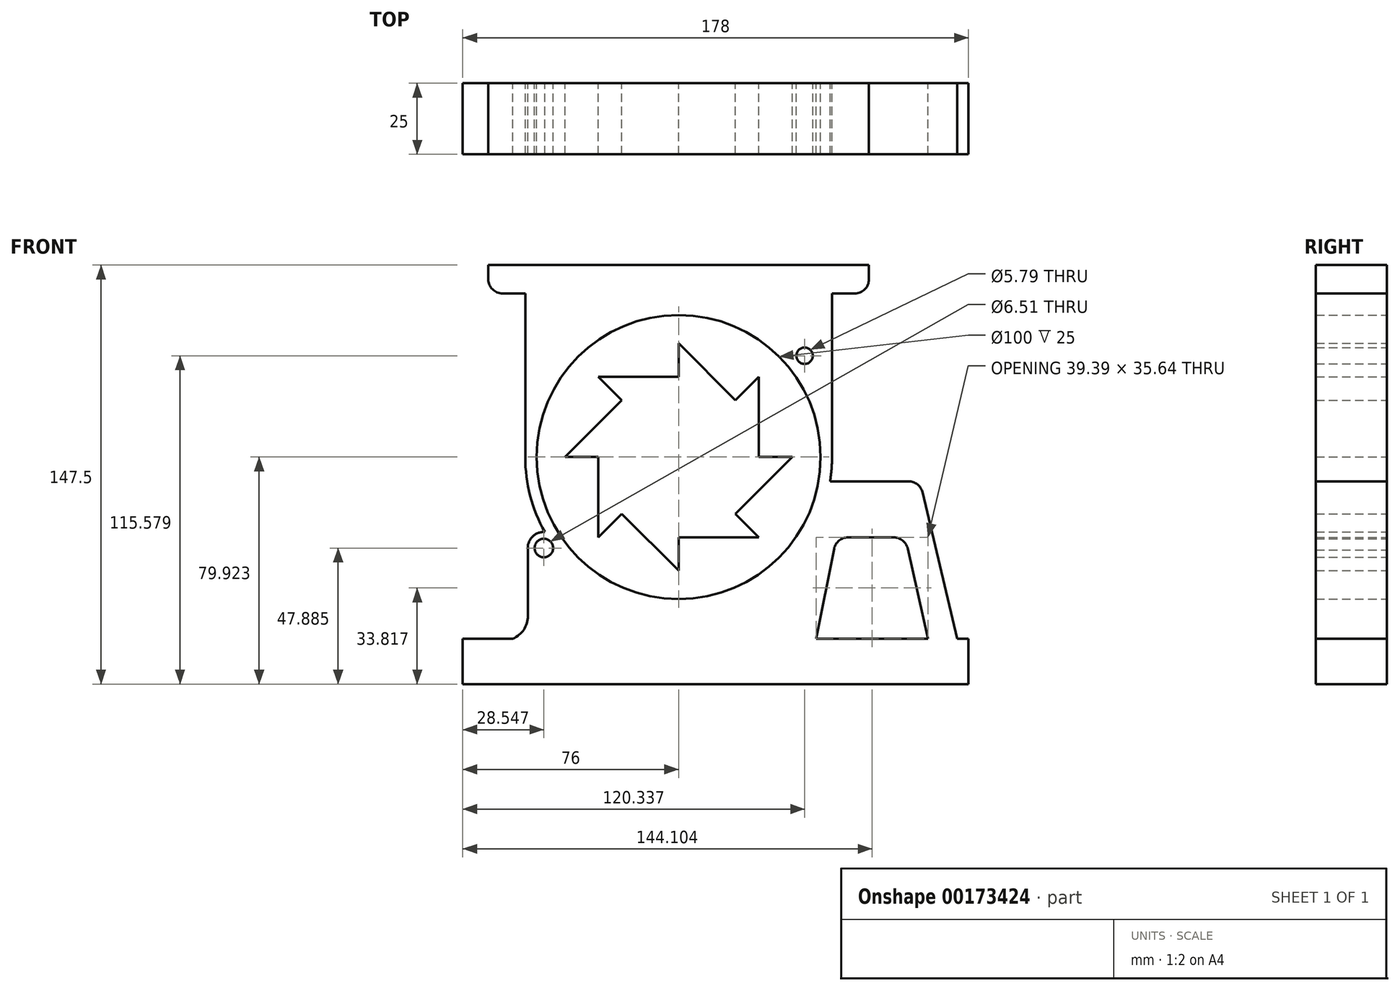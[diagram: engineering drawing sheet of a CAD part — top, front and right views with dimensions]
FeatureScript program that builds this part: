
annotation { "Feature Type Name" : "Feature", "Feature Type Description" : "" }
export const myFeature = defineFeature(function(context is Context, id is Id, definition is map)
    precondition{}
    {
        {
            var Q0;
            Q0=qCreatedBy(makeId("Front.planeOp"),FACE);
            var sketch = newSketch(context, id + "F0", { "sketchPlane" : qUnion([Q0])});
            skLineSegment(sketch, "E0.bottom", {"start": v(-56, -73.91) * mm, "end": v(122, -73.91) * mm});
            skLineSegment(sketch, "E0.top", {"start": v(-56, -57.91) * mm, "end": v(122, -57.91) * mm});
            skLineSegment(sketch, "E0.left", {"start": v(-56, -73.91) * mm, "end": v(-56, -57.91) * mm});
            skLineSegment(sketch, "E0.right", {"start": v(122, -73.91) * mm, "end": v(122, -57.91) * mm});
            skLineSegment(sketch, "E1", {"start": v(20, -57.91) * mm, "end": v(20, -45.15) * mm});
            skLineSegment(sketch, "E2", {"start": v(0, -57.91) * mm, "end": v(0, -44.15) * mm});
            skLineSegment(sketch, "E3", {"start": v(40, -57.91) * mm, "end": v(40, -44.15) * mm});
            skArc(sketch, "E4", {"start": v(-15.7, -34.5) * mm, "mid": v(54, -35.93) * mm, "end": v(67.02, 32.57) * mm});
            skArc(sketch, "E5.trimOffspring", {"start": v(56.51, 45.8) * mm, "mid": v(-13.14, 48.65) * mm, "end": v(-27.56, -19.56) * mm});
            skCircle(sketch, "E6", {"center": v(20, 6.01) * mm, "radius": 50 * mm});
            skCircle(sketch, "E7", {"center": v(20, 6.01) * mm, "radius": 10 * mm});
            skLineSegment(sketch, "E8", {"start": v(20, 16.01) * mm, "end": v(20, 46.01) * mm});
            skLineSegment(sketch, "E9", {"start": v(30, 6.01) * mm, "end": v(60, 6.01) * mm});
            skLineSegment(sketch, "E10", {"start": v(20, -3.99) * mm, "end": v(20, -33.99) * mm});
            skLineSegment(sketch, "E11", {"start": v(10, 6.01) * mm, "end": v(-20, 6.01) * mm});
            skLineSegment(sketch, "E12", {"start": v(27.07, 13.08) * mm, "end": v(48.28, 34.3) * mm});
            skLineSegment(sketch, "E13", {"start": v(27.07, -1.06) * mm, "end": v(48.28, -22.27) * mm});
            skLineSegment(sketch, "E14", {"start": v(12.93, -1.06) * mm, "end": v(-8.28, -22.27) * mm});
            skLineSegment(sketch, "E15", {"start": v(12.93, 13.08) * mm, "end": v(-8.28, 34.3) * mm});
            skLineSegment(sketch, "E16", {"start": v(48.28, 34.3) * mm, "end": v(48.28, 6.01) * mm});
            skLineSegment(sketch, "E17", {"start": v(20, 46.01) * mm, "end": v(40, 26.01) * mm});
            skLineSegment(sketch, "E18", {"start": v(60, 6.01) * mm, "end": v(40, -13.99) * mm});
            skLineSegment(sketch, "E19", {"start": v(48.28, -22.27) * mm, "end": v(20, -22.27) * mm});
            skLineSegment(sketch, "E20", {"start": v(20, -33.99) * mm, "end": v(0, -13.99) * mm});
            skLineSegment(sketch, "E21", {"start": v(-8.28, -22.27) * mm, "end": v(-8.28, 6.01) * mm});
            skPoint(sketch, "E21.endSnap0", {"position": v(-5, 6.01) * mm});
            skPoint(sketch, "E22.endSnap0", {"position": v(2.32, 23.7) * mm});
            skLineSegment(sketch, "E23", {"start": v(-8.28, 34.3) * mm, "end": v(20, 34.3) * mm});
            skLineSegment(sketch, "E24", {"start": v(-20, 6.01) * mm, "end": v(0, 26.01) * mm});
            skArc(sketch, "E25", {"start": v(-27.56, -19.56) * mm, "mid": v(1.53, -44.73) * mm, "end": v(40, -44.15) * mm});
            skArc(sketch, "E26.trimOffspring", {"start": v(67.02, 32.57) * mm, "mid": v(65.84, 34.55) * mm, "end": v(64.58, 36.49) * mm});
            skLineSegment(sketch, "E27", {"start": v(-34, 6.01) * mm, "end": v(-34, 63.59) * mm});
            skLineSegment(sketch, "E28", {"start": v(-34, 63.59) * mm, "end": v(74, 63.59) * mm});
            skLineSegment(sketch, "E29", {"start": v(74, 6.01) * mm, "end": v(74, 63.59) * mm});
            skLineSegment(sketch, "E30.bottom", {"start": v(-42, 63.59) * mm, "end": v(82, 63.59) * mm});
            skLineSegment(sketch, "E30.top", {"start": v(-47, 73.59) * mm, "end": v(87, 73.59) * mm});
            skLineSegment(sketch, "E30.left", {"start": v(-47, 68.59) * mm, "end": v(-47, 73.59) * mm});
            skLineSegment(sketch, "E30.right", {"start": v(87, 68.59) * mm, "end": v(87, 73.59) * mm});
            skLineSegment(sketch, "E31", {"start": v(20, 73.59) * mm, "end": v(20, 83.54) * mm});
            skPoint(sketch, "E32.visualSharp", {"position": v(-47, 63.59) * mm});
            skArc(sketch, "E32.filletArc", {"start": v(-47, 68.59) * mm, "mid": v(-45.54, 65.05) * mm, "end": v(-42, 63.59) * mm});
            skPoint(sketch, "E33.visualSharp", {"position": v(87, 63.59) * mm});
            skArc(sketch, "E33.filletArc", {"start": v(82, 63.59) * mm, "mid": v(85.54, 65.05) * mm, "end": v(87, 68.59) * mm});
            skCircle(sketch, "E34", {"center": v(64.34, 41.67) * mm, "radius": 2.9 * mm});
            skArc(sketch, "E35", {"start": v(64.58, 36.49) * mm, "mid": v(68.38, 44.92) * mm, "end": v(59.33, 43.02) * mm});
            skArc(sketch, "E36.trimOffspring", {"start": v(59.33, 43.02) * mm, "mid": v(57.95, 44.43) * mm, "end": v(56.51, 45.8) * mm});
            skCircle(sketch, "E37", {"center": v(-27.45, -26.02) * mm, "radius": 3.26 * mm});
            skArc(sketch, "E38", {"start": v(-27.12, -20.37) * mm, "mid": v(-32.15, -29.2) * mm, "end": v(-22.08, -27.83) * mm});
            skLineSegment(sketch, "E39", {"start": v(-33.08, -26.7) * mm, "end": v(-33.08, -50) * mm});
            skArc(sketch, "E40", {"start": v(-38.33, -57.91) * mm, "mid": v(-34.51, -54.74) * mm, "end": v(-33.08, -50) * mm});
            skLineSegment(sketch, "E41", {"start": v(68.4, -57.91) * mm, "end": v(74.72, -26.3) * mm});
            skPoint(sketch, "E41.endSnap0", {"position": v(34.14, -22.27) * mm});
            skLineSegment(sketch, "E42", {"start": v(79.63, -22.27) * mm, "end": v(95.74, -22.27) * mm});
            skLineSegment(sketch, "E43", {"start": v(100.61, -26.17) * mm, "end": v(107.8, -57.91) * mm});
            skLineSegment(sketch, "E44", {"start": v(118.1, -57.91) * mm, "end": v(105.84, -6.41) * mm});
            skLineSegment(sketch, "E45", {"start": v(100.98, -2.57) * mm, "end": v(73.31, -2.57) * mm});
            skPoint(sketch, "E46.visualSharp", {"position": v(75.53, -22.27) * mm});
            skArc(sketch, "E46.filletArc", {"start": v(79.63, -22.27) * mm, "mid": v(76.46, -23.4) * mm, "end": v(74.72, -26.3) * mm});
            skPoint(sketch, "E47.visualSharp", {"position": v(99.73, -22.27) * mm});
            skArc(sketch, "E47.filletArc", {"start": v(100.61, -26.17) * mm, "mid": v(98.86, -23.36) * mm, "end": v(95.74, -22.27) * mm});
            skPoint(sketch, "E48.visualSharp", {"position": v(104.93, -2.57) * mm});
            skArc(sketch, "E48.filletArc", {"start": v(105.84, -6.41) * mm, "mid": v(104.08, -3.64) * mm, "end": v(100.98, -2.57) * mm});
            skSolve(sketch);
        }
        {
            var Q0;
            Q0 = qSketchRegion(id + "F0", true);
            var Q1;
            {var subQ3=sQuery(id+"F0.wireOp",EDGE,"E18");Q1=makeQuery(id+"F0.imprint","IMPRINT",FACE,{"disambiguationData":[TD([[makeQuery(id+"F0.imprint","IMPRINT",EDGE,{"derivedFrom":subQ3}),-1.0]])]});}
            var Q2;
            {var subQ0=sQuery(id+"F0.wireOp",EDGE,"E19");Q2=makeQuery(id+"F0.imprint","IMPRINT",FACE,{"disambiguationData":[TD([[makeQuery(id+"F0.imprint","IMPRINT",EDGE,{"derivedFrom":subQ0}),-1.0]])]});}
            var Q3;
            {var subQ0=sQuery(id+"F0.wireOp",EDGE,"E20");Q3=makeQuery(id+"F0.imprint","IMPRINT",FACE,{"disambiguationData":[TD([[makeQuery(id+"F0.imprint","IMPRINT",EDGE,{"derivedFrom":subQ0}),-1.0]])]});}
            var Q4;
            {var subQ0=sQuery(id+"F0.wireOp",EDGE,"E21");Q4=makeQuery(id+"F0.imprint","IMPRINT",FACE,{"disambiguationData":[TD([[makeQuery(id+"F0.imprint","IMPRINT",EDGE,{"derivedFrom":subQ0}),-1.0]])]});}
            var Q5;
            {var subQ3=sQuery(id+"F0.wireOp",EDGE,"E24");Q5=makeQuery(id+"F0.imprint","IMPRINT",FACE,{"disambiguationData":[TD([[makeQuery(id+"F0.imprint","IMPRINT",EDGE,{"derivedFrom":subQ3}),-1.0]])]});}
            var Q6;
            {var subQ0=sQuery(id+"F0.wireOp",EDGE,"E23");Q6=makeQuery(id+"F0.imprint","IMPRINT",FACE,{"disambiguationData":[TD([[makeQuery(id+"F0.imprint","IMPRINT",EDGE,{"derivedFrom":subQ0}),-1.0]])]});}
            var Q7;
            {var subQ0=sQuery(id+"F0.wireOp",EDGE,"E17");Q7=makeQuery(id+"F0.imprint","IMPRINT",FACE,{"disambiguationData":[TD([[makeQuery(id+"F0.imprint","IMPRINT",EDGE,{"derivedFrom":subQ0}),-1.0]])]});}
            var Q8;
            {var subQ0=sQuery(id+"F0.wireOp",EDGE,"E16");Q8=makeQuery(id+"F0.imprint","IMPRINT",FACE,{"disambiguationData":[TD([[makeQuery(id+"F0.imprint","IMPRINT",EDGE,{"derivedFrom":subQ0}),-1.0]])]});}
            var Q9;
            {var subQ0=sQuery(id+"F0.wireOp",EDGE,"E7");var subQ4=makeQuery(id+"F0.imprint","INTERSECT",VERTEX,{"derivedFrom":[subQ0,sQuery(id+"F0.wireOp",EDGE,"E8")]});Q9=makeQuery(id+"F0.imprint","IMPRINT",FACE,{"disambiguationData":[TD([[makeQuery(id+"F0.imprint","IMPRINT",EDGE,{"disambiguationData":[TD([[subQ4,1.0]])],"derivedFrom":subQ0}),1.0]])]});}
            var Q10;
            {var subQ3=sQuery(id+"F0.wireOp",EDGE,"E2");Q10=makeQuery(id+"F0.imprint","IMPRINT",FACE,{"disambiguationData":[TD([[makeQuery(id+"F0.imprint","IMPRINT",EDGE,{"derivedFrom":subQ3}),-1.0]])]});}
            var Q11;
            {var subQ3=sQuery(id+"F0.wireOp",EDGE,"E3");Q11=makeQuery(id+"F0.imprint","IMPRINT",FACE,{"disambiguationData":[TD([[makeQuery(id+"F0.imprint","IMPRINT",EDGE,{"derivedFrom":subQ3}),1.0]])]});}
            extrude(context, id + "F1", {"entities" : qUnion([Q0, Q1, Q2, Q3, Q4, Q5, Q6, Q7, Q8, Q9, Q10, Q11]), "depth" : 25 * mm});
        }
    });
